# Revit family: Sanitary_Shower-Trays_Sanindusa_Stepin_Shower-Tray-100x80
name_source: partatom
category: Plumbing Fixtures
revit_build: Autodesk Revit 2018 (Build: 20170223_1515(x64)
units: mm (PartAtom-declared; Revit-internal decimal feet)

## family parameters
Cut with Voids When Loaded = No
Host = Face
Part Type = Normal
Room Calculation Point = No
Round Connector Dimension = Use Diameter
Shared = No

## types (1)
- Sanitary_Shower-Trays_Sanindusa_Stepin_Shower-Tray-100x80
    AssetType = Fixed
    CodePerformance = EN 14527:2006 / A1:2010 CL 2; NF EN 14527; NF EN 251; NFD11-124; NF D14-605
    Color = white
    Constituents = 48711-90 shower tray drain (not included)
    Default Elevation = 1219 mm
    Description = Installation or waste water appliance that emits a spray of water to wash the human body (BS6100)
    DrainSize = 90 mm  [stored 0.295276 ft]
    Element Type = SHOWER: Installation or waste water appliance that emits a spray of water to wash the human body (BS6100)
    Features = Extra flat shower tray that allows easy accessibility to the shower area. Glazed on all sides, except on the basis of settlement.
    Finish = gloss
    HasTray = TRUE
    Installation Instructions = https://www.tec.sanindusa.pt
    InstallationDate = 1900-12-31T23:59:59
    Manufacturer = Sanindusa
    ManufacturerName = Sanindusa
    ManufacturerURL = www.tec.sanindusa.pt
    Material = Fine Fireclay
    Model = 107542004
    ModelNumber = 107542004
    ModelReference = Stepin
    MountingType = Inset/AboveTheFloor
    Name = 100x80x3 stepin shower tray
    NominalHeight = 30 mm  [stored 0.0984252 ft]
    NominalLength = 1000 mm  [stored 3.28084 ft]
    NominalWidth = 800 mm  [stored 2.62467 ft]
    Non-slip surface = FALSE
    Pre-defined type (IFC) = SHOWER
    ProductInformation = https://www.tec.sanindusa.pt
    ProductionYear = 2019
    Shape = rectangular
    Size = 100x80
    Type (IFC) = IfcSanitaryTerminalType
    URL = www.tec.sanindusa.pt
    Uniclass2015Code = Pr_40_20_06_84
    Uniclass2015Title = Shower trays
    Uniclass2015Version = Products v1.6
    Version = 2
    WarrantyDescription = https://www.tec.sanindusa.pt
    WarrantyDurationParts = 5
    WarrantyStartDate = 1900-12-31T23:59:59
    Waste Connection = Yes
    Weight = 26.00 kg

note: [stored X ft] marks values corroborated as IEEE doubles in the binary element streams (Revit-internal decimal feet)

## geometry (parser evidence)
native form markers: Sweep x7
no freeform markers — native parametric forms only
